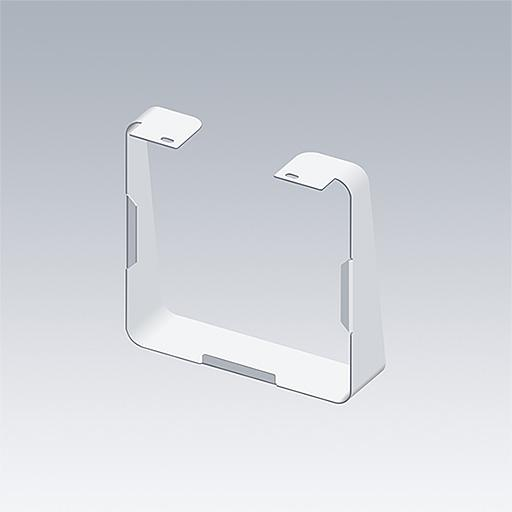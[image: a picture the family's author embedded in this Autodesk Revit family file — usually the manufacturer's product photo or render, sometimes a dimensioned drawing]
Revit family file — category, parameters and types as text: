
# Revit family: Thorn Caelon S20i
name_source: partatom
category: Lighting Fixtures
units: mm (PartAtom-declared; Revit-internal decimal feet)

## family parameters
Cut with Voids When Loaded = No
Host = Face
Light Source = No
Maintain Annotation Orientation = No
Part Type = Normal
Room Calculation Point = No
Round Connector Dimension = Use Diameter
Shared = No

## types (41) — shared parameters
Apparent Load = 20 VA
Assembly Code = Pr_70_70_48_75
Description = Outdoor flood and spotlight luminaires
Export Type to IFC As = IfcLightFixtureType
Has Cowl = No
Has Ground Spike = No
Lamp = LED
Luminaire Height = 210 mm  [stored 0.688976 ft]
Luminaire Length = 160 mm  [stored 0.524934 ft]
Luminaire Width = 149 mm  [stored 0.488845 ft]
Manufacturer = Thorn Lighting
Power Factor = 1
Type Bracket Black = Thorn-Parts-CAELON-Bracket-S12l : Black
Type Bracket White = Thorn-Parts-CAELON-Bracket-S12l : White
Type Cowl Black = Thorn CAELON-Accessory-S12i_S20i_S30i : CAELON S COWL/BK
Type Cowl White = Thorn CAELON-Accessory-S12i_S20i_S30i : CAELON S COWL/WH
Type Ground Spike Black = Thorn CAELON-Accessory-S12i_S20i_S30i : CAELON S12/20/30 GROUND SPIKE
Type Housing Black = Thorn-Parts-CAELON-Housing-S12l : Black
Type Housing White = Thorn-Parts-CAELON-Housing-S12l : White
Type IFC Predefined Type = DIRECTIONSOURCE
URL = https://www.thornlighting.com
Wattage = 24 VA
zero-valued in all types: Default Elevation

## per-type parameters (varying)
| type | Housing Finish Black | Housing Finish White | Model | Optic | Type Accessory Cowl | Type Bracket | Type Housing | Type Image | Type Light Source |
| CAELON S20I 2000-827 M BK 66 HF | Yes | No | 21035602 | Medium | Thorn CAELON-Accessory-S12i_S20i_S30i : CAELON S COWL/BK | Thorn-Parts-CAELON-Bracket-S12l : Black | Thorn-Parts-CAELON-Housing-S12l : Black | TLG_CAEL_F_S12i-S20I-S30i_BK.jpg | Thorn-Light Sources-CAELON S20I : CAELON S20I 2000-827 M BK 66 HF_photometric_data |
| CAELON S20I 2000-827 M BK HL 66 HF | Yes | No | 21035599 | Medium | Thorn CAELON-Accessory-S12i_S20i_S30i : CAELON S COWL/BK | Thorn-Parts-CAELON-Bracket-S12l : Black | Thorn-Parts-CAELON-Housing-S12l : Black | TLG_CAEL_F_S12i-S20I-S30i_BK.jpg | Thorn-Light Sources-CAELON S20I : CAELON S20I 2000-827 M BK HL 66 HF_photometric_data |
| CAELON S20I 2000-827 M WH 66 HF | No | Yes | 21035608 | Medium | Thorn CAELON-Accessory-S12i_S20i_S30i : CAELON S COWL/WH | Thorn-Parts-CAELON-Bracket-S12l : White | Thorn-Parts-CAELON-Housing-S12l : White | TLG_CAEL_F_S12i-S20I-S30i_WH.jpg | Thorn-Light Sources-CAELON S20I : CAELON S20I 2000-827 M WH 66 HF_photometric_data |
| CAELON S20I 2000-827 M WH HL 66 HF | No | Yes | 21035605 | Medium | Thorn CAELON-Accessory-S12i_S20i_S30i : CAELON S COWL/WH | Thorn-Parts-CAELON-Bracket-S12l : White | Thorn-Parts-CAELON-Housing-S12l : White | TLG_CAEL_F_S12i-S20I-S30i_WH.jpg | Thorn-Light Sources-CAELON S20I : CAELON S20I 2000-827 M WH HL 66 HF_photometric_data |
| CAELON S20I 2000-827 N BK 66 HF | Yes | No | 21034132 | Narrow | Thorn CAELON-Accessory-S12i_S20i_S30i : CAELON S COWL/BK | Thorn-Parts-CAELON-Bracket-S12l : Black | Thorn-Parts-CAELON-Housing-S12l : Black | TLG_CAEL_F_S12i-S20I-S30i_BK.jpg | Thorn-Light Sources-CAELON S20I : CAELON S20I 2000-827 N BK 66 HF_photometric_data |
| CAELON S20I 2000-827 N BK HL 66 HF | Yes | No | 21034129 | Narrow | Thorn CAELON-Accessory-S12i_S20i_S30i : CAELON S COWL/BK | Thorn-Parts-CAELON-Bracket-S12l : Black | Thorn-Parts-CAELON-Housing-S12l : Black | TLG_CAEL_F_S12i-S20I-S30i_BK.jpg | Thorn-Light Sources-CAELON S20I : CAELON S20I 2000-827 N BK HL 66 HF_photometric_data |
| CAELON S20I 2000-827 N WH 66 HF | No | Yes | 21034138 | Narrow | Thorn CAELON-Accessory-S12i_S20i_S30i : CAELON S COWL/WH | Thorn-Parts-CAELON-Bracket-S12l : White | Thorn-Parts-CAELON-Housing-S12l : White | TLG_CAEL_F_S12i-S20I-S30i_WH.jpg | Thorn-Light Sources-CAELON S20I : CAELON S20I 2000-827 N WH 66 HF_photometric_data |
| CAELON S20I 2000-827 N WH HL 66 HF | No | Yes | 21034135 | Narrow | Thorn CAELON-Accessory-S12i_S20i_S30i : CAELON S COWL/WH | Thorn-Parts-CAELON-Bracket-S12l : White | Thorn-Parts-CAELON-Housing-S12l : White | TLG_CAEL_F_S12i-S20I-S30i_WH.jpg | Thorn-Light Sources-CAELON S20I : CAELON S20I 2000-827 N WH HL 66 HF_photometric_data |
| CAELON S20I 2000-827 SN BK 66 HF | Yes | No | 21034120 | Super Narrow | Thorn CAELON-Accessory-S12i_S20i_S30i : CAELON S COWL/BK | Thorn-Parts-CAELON-Bracket-S12l : Black | Thorn-Parts-CAELON-Housing-S12l : Black | TLG_CAEL_F_S12i-S20I-S30i_BK.jpg | Thorn-Light Sources-CAELON S20I : CAELON S20I 2000-827 SN BK 66 HF_photometric_data |
| CAELON S20I 2000-827 SN BK HL 66 HF | Yes | No | 21034117 | Super Narrow | Thorn CAELON-Accessory-S12i_S20i_S30i : CAELON S COWL/BK | Thorn-Parts-CAELON-Bracket-S12l : Black | Thorn-Parts-CAELON-Housing-S12l : Black | TLG_CAEL_F_S12i-S20I-S30i_BK.jpg | Thorn-Light Sources-CAELON S20I : CAELON S20I 2000-827 SN BK HL 66 HF_photometric_data |
| CAELON S20I 2000-827 SN WH 66 HF | No | Yes | 21034126 | Super Narrow | Thorn CAELON-Accessory-S12i_S20i_S30i : CAELON S COWL/WH | Thorn-Parts-CAELON-Bracket-S12l : White | Thorn-Parts-CAELON-Housing-S12l : White | TLG_CAEL_F_S12i-S20I-S30i_WH.jpg | Thorn-Light Sources-CAELON S20I : CAELON S20I 2000-827 SN WH 66 HF_photometric_data |
| CAELON S20I 2000-827 SN WH HL 66 HF | No | Yes | 21034123 | Super Narrow | Thorn CAELON-Accessory-S12i_S20i_S30i : CAELON S COWL/WH | Thorn-Parts-CAELON-Bracket-S12l : White | Thorn-Parts-CAELON-Housing-S12l : White | TLG_CAEL_F_S12i-S20I-S30i_WH.jpg | Thorn-Light Sources-CAELON S20I : CAELON S20I 2000-827 SN WH HL 66 HF_photometric_data |
| CAELON S20I 2000-827 W BK 66 HF | Yes | No | 21034141 | Wide | Thorn CAELON-Accessory-S12i_S20i_S30i : CAELON S COWL/BK | Thorn-Parts-CAELON-Bracket-S12l : Black | Thorn-Parts-CAELON-Housing-S12l : Black | TLG_CAEL_F_S12i-S20I-S30i_BK.jpg | Thorn-Light Sources-CAELON S20I : CAELON S20I 2000-827 W BK 66 HF_photometric_data |
| CAELON S20I 2000-827 W WH 66 HF | No | Yes | 21034144 | Wide | Thorn CAELON-Accessory-S12i_S20i_S30i : CAELON S COWL/WH | Thorn-Parts-CAELON-Bracket-S12l : White | Thorn-Parts-CAELON-Housing-S12l : White | TLG_CAEL_F_S12i-S20I-S30i_WH.jpg | Thorn-Light Sources-CAELON S20I : CAELON S20I 2000-827 W WH 66 HF_photometric_data |
| CAELON S20I 2000-830 M BK 66 HF | Yes | No | 21035614 | Medium | Thorn CAELON-Accessory-S12i_S20i_S30i : CAELON S COWL/BK | Thorn-Parts-CAELON-Bracket-S12l : Black | Thorn-Parts-CAELON-Housing-S12l : Black | TLG_CAEL_F_S12i-S20I-S30i_BK.jpg | Thorn-Light Sources-CAELON S20I : CAELON S20I 2000-830 M BK 66 HF_photometric_data |
| CAELON S20I 2000-830 M BK HL 66 HF | Yes | No | 21035611 | Medium | Thorn CAELON-Accessory-S12i_S20i_S30i : CAELON S COWL/BK | Thorn-Parts-CAELON-Bracket-S12l : Black | Thorn-Parts-CAELON-Housing-S12l : Black | TLG_CAEL_F_S12i-S20I-S30i_BK.jpg | Thorn-Light Sources-CAELON S20I : CAELON S20I 2000-830 M BK HL 66 HF_photometric_data |
| CAELON S20I 2000-830 M WH 66 HF | No | Yes | 21035620 | Medium | Thorn CAELON-Accessory-S12i_S20i_S30i : CAELON S COWL/WH | Thorn-Parts-CAELON-Bracket-S12l : White | Thorn-Parts-CAELON-Housing-S12l : White | TLG_CAEL_F_S12i-S20I-S30i_WH.jpg | Thorn-Light Sources-CAELON S20I : CAELON S20I 2000-830 M WH 66 HF_photometric_data |
| CAELON S20I 2000-830 M WH HL 66 HF | No | Yes | 21035617 | Medium | Thorn CAELON-Accessory-S12i_S20i_S30i : CAELON S COWL/WH | Thorn-Parts-CAELON-Bracket-S12l : White | Thorn-Parts-CAELON-Housing-S12l : White | TLG_CAEL_F_S12i-S20I-S30i_WH.jpg | Thorn-Light Sources-CAELON S20I : CAELON S20I 2000-830 M WH HL 66 HF_photometric_data |
| CAELON S20I 2000-830 N BK 66 HF | Yes | No | 21034164 | Narrow | Thorn CAELON-Accessory-S12i_S20i_S30i : CAELON S COWL/BK | Thorn-Parts-CAELON-Bracket-S12l : Black | Thorn-Parts-CAELON-Housing-S12l : Black | TLG_CAEL_F_S12i-S20I-S30i_BK.jpg | Thorn-Light Sources-CAELON S20I : CAELON S20I 2000-830 N BK 66 HF_photometric_data |
| CAELON S20I 2000-830 N BK HL 66 HF | Yes | No | 21034161 | Narrow | Thorn CAELON-Accessory-S12i_S20i_S30i : CAELON S COWL/BK | Thorn-Parts-CAELON-Bracket-S12l : Black | Thorn-Parts-CAELON-Housing-S12l : Black | TLG_CAEL_F_S12i-S20I-S30i_BK.jpg | Thorn-Light Sources-CAELON S20I : CAELON S20I 2000-830 N BK HL 66 HF_photometric_data |
| CAELON S20I 2000-830 N WH 66 HF | No | Yes | 21034170 | Narrow | Thorn CAELON-Accessory-S12i_S20i_S30i : CAELON S COWL/WH | Thorn-Parts-CAELON-Bracket-S12l : White | Thorn-Parts-CAELON-Housing-S12l : White | TLG_CAEL_F_S12i-S20I-S30i_WH.jpg | Thorn-Light Sources-CAELON S20I : CAELON S20I 2000-830 N WH 66 HF_photometric_data |
| CAELON S20I 2000-830 N WH HL 66 HF | No | Yes | 21034167 | Narrow | Thorn CAELON-Accessory-S12i_S20i_S30i : CAELON S COWL/WH | Thorn-Parts-CAELON-Bracket-S12l : White | Thorn-Parts-CAELON-Housing-S12l : White | TLG_CAEL_F_S12i-S20I-S30i_WH.jpg | Thorn-Light Sources-CAELON S20I : CAELON S20I 2000-830 N WH HL 66 HF_photometric_data |
| CAELON S20I 2000-830 SN BK 66 HF | Yes | No | 21034152 | Super Narrow | Thorn CAELON-Accessory-S12i_S20i_S30i : CAELON S COWL/BK | Thorn-Parts-CAELON-Bracket-S12l : Black | Thorn-Parts-CAELON-Housing-S12l : Black | TLG_CAEL_F_S12i-S20I-S30i_BK.jpg | Thorn-Light Sources-CAELON S20I : CAELON S20I 2000-830 SN BK 66 HF_photometric_data |
| CAELON S20I 2000-830 SN BK HL 66 HF | Yes | No | 21034149 | Super Narrow | Thorn CAELON-Accessory-S12i_S20i_S30i : CAELON S COWL/BK | Thorn-Parts-CAELON-Bracket-S12l : Black | Thorn-Parts-CAELON-Housing-S12l : Black | TLG_CAEL_F_S12i-S20I-S30i_BK.jpg | Thorn-Light Sources-CAELON S20I : CAELON S20I 2000-830 SN BK HL 66 HF_photometric_data |
| CAELON S20I 2000-830 SN WH 66 HF | No | Yes | 21034158 | Super Narrow | Thorn CAELON-Accessory-S12i_S20i_S30i : CAELON S COWL/WH | Thorn-Parts-CAELON-Bracket-S12l : White | Thorn-Parts-CAELON-Housing-S12l : White | TLG_CAEL_F_S12i-S20I-S30i_WH.jpg | Thorn-Light Sources-CAELON S20I : CAELON S20I 2000-830 SN WH 66 HF_photometric_data |
| CAELON S20I 2000-830 SN WH HL 66 HF | No | Yes | 21034155 | Super Narrow | Thorn CAELON-Accessory-S12i_S20i_S30i : CAELON S COWL/WH | Thorn-Parts-CAELON-Bracket-S12l : White | Thorn-Parts-CAELON-Housing-S12l : White | TLG_CAEL_F_S12i-S20I-S30i_WH.jpg | Thorn-Light Sources-CAELON S20I : CAELON S20I 2000-830 SN WH HL 66 HF_photometric_data |
| CAELON S20I 2000-830 W BK 66 HF | Yes | No | 21034173 | Wide | Thorn CAELON-Accessory-S12i_S20i_S30i : CAELON S COWL/BK | Thorn-Parts-CAELON-Bracket-S12l : Black | Thorn-Parts-CAELON-Housing-S12l : Black | TLG_CAEL_F_S12i-S20I-S30i_BK.jpg | Thorn-Light Sources-CAELON S20I : CAELON S20I 2000-830 W BK 66 HF_photometric_data |
| CAELON S20I 2000-830 W WH 66 HF | No | Yes | 21034176 | Wide | Thorn CAELON-Accessory-S12i_S20i_S30i : CAELON S COWL/WH | Thorn-Parts-CAELON-Bracket-S12l : White | Thorn-Parts-CAELON-Housing-S12l : White | TLG_CAEL_F_S12i-S20I-S30i_WH.jpg | Thorn-Light Sources-CAELON S20I : CAELON S20I 2000-830 W WH 66 HF_photometric_data |
| CAELON S20I 2000-840 M BK 66 HF | Yes | No | 21035626 | Medium | Thorn CAELON-Accessory-S12i_S20i_S30i : CAELON S COWL/BK | Thorn-Parts-CAELON-Bracket-S12l : Black | Thorn-Parts-CAELON-Housing-S12l : Black | TLG_CAEL_F_S12i-S20I-S30i_BK.jpg | Thorn-Light Sources-CAELON S20I : CAELON S20I 2000-840 M BK 66 HF_photometric_data |
| CAELON S20I 2000-840 M BK HL 66 HF | Yes | No | 21035623 | Medium | Thorn CAELON-Accessory-S12i_S20i_S30i : CAELON S COWL/BK | Thorn-Parts-CAELON-Bracket-S12l : Black | Thorn-Parts-CAELON-Housing-S12l : Black | TLG_CAEL_F_S12i-S20I-S30i_BK.jpg | Thorn-Light Sources-CAELON S20I : CAELON S20I 2000-840 M BK HL 66 HF_photometric_data |
| CAELON S20I 2000-840 M WH 66 HF | No | Yes | 21035632 | Medium | Thorn CAELON-Accessory-S12i_S20i_S30i : CAELON S COWL/WH | Thorn-Parts-CAELON-Bracket-S12l : White | Thorn-Parts-CAELON-Housing-S12l : White | TLG_CAEL_F_S12i-S20I-S30i_WH.jpg | Thorn-Light Sources-CAELON S20I : CAELON S20I 2000-840 M WH 66 HF_photometric_data |
| CAELON S20I 2000-840 M WH HL 66 HF | No | Yes | 21035629 | Medium | Thorn CAELON-Accessory-S12i_S20i_S30i : CAELON S COWL/WH | Thorn-Parts-CAELON-Bracket-S12l : White | Thorn-Parts-CAELON-Housing-S12l : White | TLG_CAEL_F_S12i-S20I-S30i_WH.jpg | Thorn-Light Sources-CAELON S20I : CAELON S20I 2000-840 M WH HL 66 HF_photometric_data |
| CAELON S20I 2000-840 N BK 66 HF | Yes | No | 21034196 | Narrow | Thorn CAELON-Accessory-S12i_S20i_S30i : CAELON S COWL/BK | Thorn-Parts-CAELON-Bracket-S12l : Black | Thorn-Parts-CAELON-Housing-S12l : Black | TLG_CAEL_F_S12i-S20I-S30i_BK.jpg | Thorn-Light Sources-CAELON S20I : CAELON S20I 2000-840 N BK 66 HF_photometric_data |
| CAELON S20I 2000-840 N BK HL 66 HF | Yes | No | 21034193 | Narrow | Thorn CAELON-Accessory-S12i_S20i_S30i : CAELON S COWL/BK | Thorn-Parts-CAELON-Bracket-S12l : Black | Thorn-Parts-CAELON-Housing-S12l : Black | TLG_CAEL_F_S12i-S20I-S30i_BK.jpg | Thorn-Light Sources-CAELON S20I : CAELON S20I 2000-840 N BK HL 66 HF_photometric_data |
| CAELON S20I 2000-840 N WH 66 HF | No | Yes | 21034202 | Narrow | Thorn CAELON-Accessory-S12i_S20i_S30i : CAELON S COWL/WH | Thorn-Parts-CAELON-Bracket-S12l : White | Thorn-Parts-CAELON-Housing-S12l : White | TLG_CAEL_F_S12i-S20I-S30i_WH.jpg | Thorn-Light Sources-CAELON S20I : CAELON S20I 2000-840 N WH 66 HF_photometric_data |
| CAELON S20I 2000-840 N WH HL 66 HF | No | Yes | 21034199 | Narrow | Thorn CAELON-Accessory-S12i_S20i_S30i : CAELON S COWL/WH | Thorn-Parts-CAELON-Bracket-S12l : White | Thorn-Parts-CAELON-Housing-S12l : White | TLG_CAEL_F_S12i-S20I-S30i_WH.jpg | Thorn-Light Sources-CAELON S20I : CAELON S20I 2000-840 N WH HL 66 HF_photometric_data |
| CAELON S20I 2000-840 SN BK 66 HF | Yes | No | 21034184 | Super Narrow | Thorn CAELON-Accessory-S12i_S20i_S30i : CAELON S COWL/BK | Thorn-Parts-CAELON-Bracket-S12l : Black | Thorn-Parts-CAELON-Housing-S12l : Black | TLG_CAEL_F_S12i-S20I-S30i_BK.jpg | Thorn-Light Sources-CAELON S20I : CAELON S20I 2000-840 SN BK 66 HF_photometric_data |
| CAELON S20I 2000-840 SN BK HL 66 HF | Yes | No | 21034181 | Super Narrow | Thorn CAELON-Accessory-S12i_S20i_S30i : CAELON S COWL/BK | Thorn-Parts-CAELON-Bracket-S12l : Black | Thorn-Parts-CAELON-Housing-S12l : Black | TLG_CAEL_F_S12i-S20I-S30i_BK.jpg | Thorn-Light Sources-CAELON S20I : CAELON S20I 2000-840 SN BK HL 66 HF_photometric_data |
| CAELON S20I 2000-840 SN WH 66 HF | No | Yes | 21034190 | Super Narrow | Thorn CAELON-Accessory-S12i_S20i_S30i : CAELON S COWL/WH | Thorn-Parts-CAELON-Bracket-S12l : White | Thorn-Parts-CAELON-Housing-S12l : White | TLG_CAEL_F_S12i-S20I-S30i_WH.jpg | Thorn-Light Sources-CAELON S20I : CAELON S20I 2000-840 SN WH 66 HF_photometric_data |
| CAELON S20I 2000-840 SN WH HL 66 HF | No | Yes | 21034187 | Super Narrow | Thorn CAELON-Accessory-S12i_S20i_S30i : CAELON S COWL/WH | Thorn-Parts-CAELON-Bracket-S12l : White | Thorn-Parts-CAELON-Housing-S12l : White | TLG_CAEL_F_S12i-S20I-S30i_WH.jpg | Thorn-Light Sources-CAELON S20I : CAELON S20I 2000-840 SN WH HL 66 HF_photometric_data |
| CAELON S20I 2000-840 W BK 66 HF | Yes | No | 21034205 | Wide | Thorn CAELON-Accessory-S12i_S20i_S30i : CAELON S COWL/BK | Thorn-Parts-CAELON-Bracket-S12l : Black | Thorn-Parts-CAELON-Housing-S12l : Black | TLG_CAEL_F_S12i-S20I-S30i_BK.jpg | Thorn-Light Sources-CAELON S20I : CAELON S20I 2000-840 W BK 66 HF_photometric_data |

note: [stored X ft] marks values corroborated as IEEE doubles in the binary element streams (Revit-internal decimal feet)

## geometry (parser evidence)
native form markers: Sweep x12
no freeform markers — native parametric forms only
